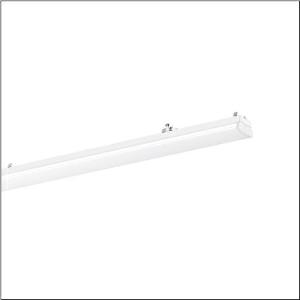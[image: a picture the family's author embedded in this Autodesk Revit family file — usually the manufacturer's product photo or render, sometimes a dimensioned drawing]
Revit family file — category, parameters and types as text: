
# Revit family: licross_11_recessed_opal_mo_51tl1dcn485g
name_source: partatom
category: Lighting Fixtures
units: mm (PartAtom-declared; Revit-internal decimal feet)

## family parameters
Cut with Voids When Loaded = No
Host = Face
Light Source = No
Part Type = Normal
Room Calculation Point = No
Round Connector Dimension = Use Diameter
Shared = No

## types (1)
- --- (1 x LED, 8820 lm, 49.3 W, 4000K)
    Apparent Load = 49 VA
    CIE Flux Codes = 44 73 91 87 100
    Color Rendering = 80
    Color Temperature = 4000K
    Default Elevation = 1800 mm
    Description = Licross 11 recessed opal MO, luminaire insert, of sheet steel, coil coated, white, length: 1.500mm, width: 76mm, height: 87mm, LED rated luminous flux: 8.820lm, light colour: 840, SDCM (Standard Deviation of Colour Matching)MacAdam ≤ 2 SDCM (initial), control gear: ON/OFF Multilumen, CLOi, with plug, 3-pole, with phase selection, mains connection: 220..240V, AC, 50/60Hz, start of lifetime: 49W, end of service life: 55W, internal wiring halogen-free, primary optical cover: cover, of PMMA, light emission: direct with ceiling illumination distribution, primary light characteristic: symmetric, protection rating (complete): IP40, insulation class (complete): insulation class I (protective earthing), certification: CE, ENEC, VDE, UKCA, protection symbol: D if used in an environment without relevant dust loads with corresponding accessories, impact resistance: IK06, permissible ambient temperature for indoor applications: -35..+40°C, corresponds to IFS (International Featured Standards) requirements for safety and quality in the food industry, reducing of maximum allowable ambient temperature of 5°C with ceiling mounting, LABS conformity tested according to VDMA 24364:2018-05, The light source and the operating device comply with the requirements of the Ecodesign Regulation (EU) 2019/2020 and are replaceable in accordance with this regulation, packaging unit: 1 piece
    Height = 83 mm
    Lamp = 1 x LED
    Lamp Light Flux = 8820 lm
    Lamp Power = 49.3 W
    Lamp count = 1
    Length = 1500 mm
    Luminous efficacy = 179 lm/W
    Manufacturer = Siteco
    ModVariant = No
    Model = 51TL1DCN485G
    Mounting Place = Ceiling
    Mounting Type = Pendant
    Number of Poles = 1
    OnlyDefault = Yes
    Power Factor = 1
    Product Name = Licross 11 recessed opal MO
    Product group = luminaire insert | ceiling pendant
    ProductGroupID = 901
    Protection Class = Protection class I
    Protection Degree = IP 40
    RLX_Detail_Level = 1
    RLX_Emergency_Light_Flux = 0 lm
    RLX_Emergency_Type = 0
    RLX_Emergency_Type_DB = No
    RlxData = <blob elided: 24785 chars, md5=b1f3ae67>
    Socket = socket
    Standby Power = 0 W
    System Light Flux = 8820 lm
    System Power = 49 W
    Type Comments = factory setting: luminous flux: 100 % | (A | C | E) | 113 mA
    Type Image = l_1313666.jpg
    URL = http://relux.com
    VarID = @adj_001771
    Voltage = 0 V
    Weight = 0.00 kg
    Width = 76 mm

## geometry (parser evidence)
native form markers: Blend x4, Sweep x12
no freeform markers — native parametric forms only
